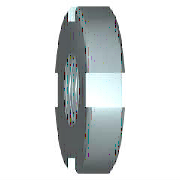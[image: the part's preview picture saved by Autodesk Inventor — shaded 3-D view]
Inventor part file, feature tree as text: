
AUTODESK INVENTOR PART (.ipt)
format: ipt  version: 2020 (Build 240168000, 168)  size: 196,096 bytes
history: native  units: mm (DEFAULTED — no unit token found)
features: sketch x3, other x2, hole x1, extrude x1, pattern_circular x1, plane x1
ambient origin geometry x8: Origin, YZ Plane, XZ Plane, XY Plane, X Axis, Y Axis, Z Axis, Center Point
bodies: Solid1 (feature_tree)
feature tree (9):
  other  "轴承体"
  hole  "螺纹"  [1 undecoded]
  extrude  "沟槽1"  Depth=10.0mm
  pattern_circular  "IDS_ARRAYGROOVE{1}"  Angle=45.0deg  [1 undecoded]
  other  "Work Axis1"
  plane  "Work Plane1"
  sketch  "草图1"  dims[d0=90.0deg d1=85.0mm]
  sketch  "草图2"  dims[d2=10.0mm]
  sketch  "草图3"  dims[d3=61.835mm d4=6.0mm d5=4.0mm d6=2.0mm d7=14.3117mm d8=8.0mm d9=0.0mm d10=1.0mm d11=45.0deg d12=4.0mm d13=4.0mm d14=39.0mm d23=10.0mm d15=0.0mm d16=40.0mm d17=360.0deg d18=1.6mm d19=30.0deg d20=1.6mm d21=30.0deg d22=0.0mm d24=0.0mm d25=1.0mm d27=45.0deg d28=0.0mm d41=1.0mm d42=1.0mm d43=1.6mm d44=1.6mm d45=90.0deg d46=0.0mm]
note: 2 required parameter values undecoded (feature->parameter linkage not recoverable at this tier; creation-order binding heuristic only, values carry confidence <= 0.55)
